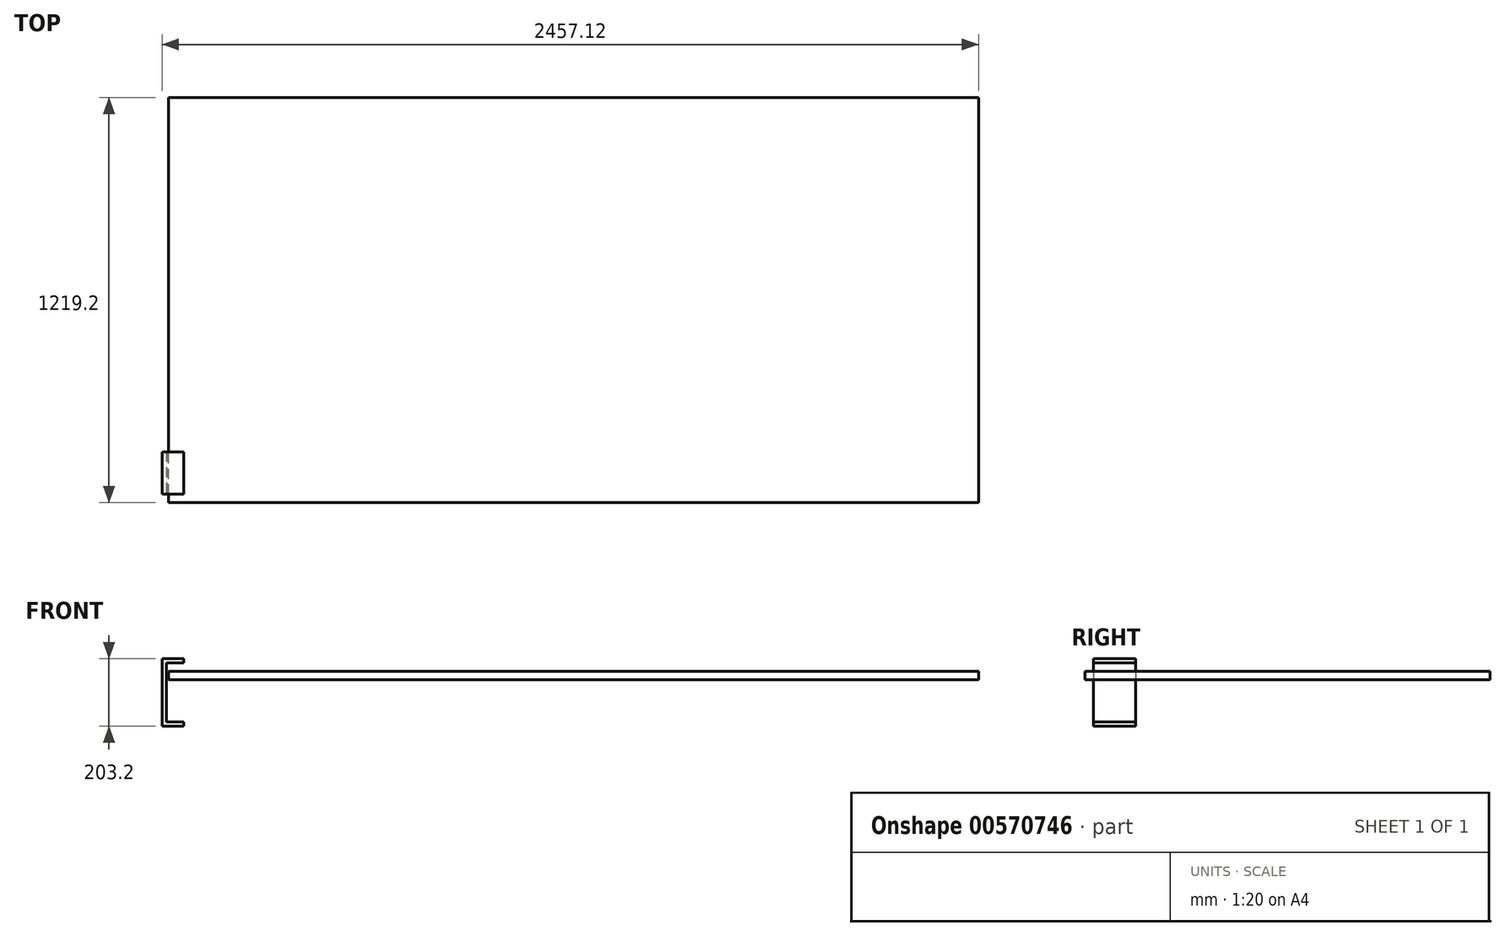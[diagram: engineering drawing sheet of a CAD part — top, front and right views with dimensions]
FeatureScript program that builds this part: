
annotation { "Feature Type Name" : "Feature", "Feature Type Description" : "" }
export const myFeature = defineFeature(function(context is Context, id is Id, definition is map)
    precondition{}
    {
        {
            var Q0;
            Q0=qCreatedBy(makeId("Top.planeOp"),FACE);
            var sketch = newSketch(context, id + "F0", { "sketchPlane" : qUnion([Q0])});
            skLineSegment(sketch, "E0.bottom", {"start": v(1219.2, -571.6) * mm, "end": v(-1219.2, -571.6) * mm});
            skLineSegment(sketch, "E0.top", {"start": v(1219.2, 647.6) * mm, "end": v(-1219.2, 647.6) * mm});
            skLineSegment(sketch, "E0.left", {"start": v(1219.2, -571.6) * mm, "end": v(1219.2, 647.6) * mm});
            skLineSegment(sketch, "E0.right", {"start": v(-1219.2, -571.6) * mm, "end": v(-1219.2, 647.6) * mm});
            skPoint(sketch, "E0.middle", {"position": v(0, 38) * mm});
            skSolve(sketch);
        }
        {
            var Q0;
            Q0=makeQuery(id+"F0.imprint","IMPRINT",FACE,{"disambiguationData":[TD([[makeQuery(id+"F0.imprint","IMPRINT",EDGE,{"derivedFrom":sQuery(id+"F0.wireOp",EDGE,"E0.bottom")}),-1.0]])]});
            extrude(context, id + "F1", {"entities" : qUnion([Q0]), "depth" : 25.4 * mm, "offsetDistance" : 25.4 * mm});
        }
        {
            var Q0;
            Q0=makeQuery(id+"F1.opExtrude","SWEPT_FACE",FACE,{"disambiguationData":[OSD([sQuery(id+"F0.wireOp",EDGE,"E0.bottom")])]});
            cPlane(context, id + "F2", {"entities" : qUnion([Q0]), "cplaneType" : CPlaneType.OFFSET, "offset" : 25.4 * mm, "oppositeDirection" : true, "width" : 152.4 * mm, "height" : 152.4 * mm});
        }
        {
            var Q0;
            Q0=qCreatedBy(id+"F2.planeOp",FACE);
            var sketch = newSketch(context, id + "F3", { "sketchPlane" : qUnion([Q0])});
            skLineSegment(sketch, "E1.bottom", {"start": v(-1237.92, 63.17) * mm, "end": v(-1225.55, 63.17) * mm});
            skLineSegment(sketch, "E1.top", {"start": v(-1237.92, -140.03) * mm, "end": v(-1225.55, -140.03) * mm});
            skLineSegment(sketch, "E1.left", {"start": v(-1237.92, 63.17) * mm, "end": v(-1237.92, -140.03) * mm});
            skLineSegment(sketch, "E1.right", {"start": v(-1225.55, 50.8) * mm, "end": v(-1225.55, -127.66) * mm});
            skLineSegment(sketch, "E2.bottom", {"start": v(-1237.92, -140.03) * mm, "end": v(-1173.73, -140.03) * mm});
            skLineSegment(sketch, "E2.top", {"start": v(-1225.55, -127.66) * mm, "end": v(-1173.73, -127.66) * mm});
            skLineSegment(sketch, "E2.left", {"start": v(-1237.92, -140.03) * mm, "end": v(-1237.92, -127.66) * mm});
            skLineSegment(sketch, "E2.right", {"start": v(-1173.73, -140.03) * mm, "end": v(-1173.73, -127.66) * mm});
            skLineSegment(sketch, "E3.bottom", {"start": v(-1237.92, 63.17) * mm, "end": v(-1173.73, 63.17) * mm});
            skLineSegment(sketch, "E3.left", {"start": v(-1237.92, 63.17) * mm, "end": v(-1237.92, -8.05) * mm});
            skLineSegment(sketch, "E3.right", {"start": v(-1173.73, 63.17) * mm, "end": v(-1173.73, 50.8) * mm});
            skLineSegment(sketch, "E4", {"start": v(-1225.55, 50.8) * mm, "end": v(-1173.73, 50.8) * mm});
            skSolve(sketch);
        }
        {
            var Q0;
            Q0 = qSketchRegion(id + "F3", true);
            var Q1;
            Q1 = qConstructionFilter(qBodyType(qCreatedBy(id + "F3" ,EDGE), BodyType.WIRE), ConstructionObject.NO);
            extrude(context, id + "F4", {"entities" : qUnion([Q0]), "surfaceEntities" : qUnion([Q1]), "oppositeDirection" : true, "depth" : 127 * mm, "offsetDistance" : 25.4 * mm});
        }
    });
